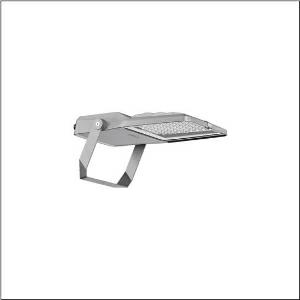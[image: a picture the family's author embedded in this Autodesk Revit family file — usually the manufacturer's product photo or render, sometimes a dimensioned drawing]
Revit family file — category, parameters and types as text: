
# Revit family: floodlight_fl_21_iq_mini___pl61_5xa7772b2c1a_d28a
name_source: partatom
category: Lighting Fixtures
units: mm (PartAtom-declared; Revit-internal decimal feet)

## family parameters
Cut with Voids When Loaded = No
Host = Face
Light Source = No
Part Type = Normal
Room Calculation Point = No
Round Connector Dimension = Use Diameter
Shared = No

## types (1)
- --- (1 x LED, 6120 lm, 45.5 W, 3000K)
    Apparent Load = 46 VA
    CIE Flux Codes = 33 65 98 100 100
    Color Rendering = 70
    Color Temperature = 3000K
    Default Elevation = 1800 mm
    Description = Floodlight FL 21 iQ mini, floodlight, primary light control with lens, of PMMA, primary optical cover: protective disc, of toughened safety glass, transparent, light distribution: PL61, light emission: direct distribution, installation type: surface-mounted, lamps: LED, High Power LED, rated values: 6.120lm | 45,5W | 134,5lm/W (begin service life); end service life: 6.120lm | 48W; at 50% lumin. flux: 3.060lm | 21,5W | 142,3lm/W, colour temperature: 3000K, colour rendering: CRI > 70, light colour: 730, light setting 1 begin service life: 100% | 6.120lm | 45,5W | 134,5lm/W | 3.000K, light setting 1 end service life: 48W, further light settings possible, control: Street-Remote, Auto-Match, Temp-Guard, Night-Set, Smart-Wire, Desk-Remote (wireless, voltage-free reading and setting of iQ features in the workshop via application-optimized NFC function/RFID function), optimised constant luminous flux control (CLO 2.0), pre-setting: linear dimming characteristic, with terminal, 6-pole, mains connection: 220..240V, AC, 50/60Hz, luminaire housing, of diecast aluminium, powder-coated, SITECO metallic grey (DB 702S), corrosivity category C5 mid according to DIN EN ISO 12944suitable for swimming poolschlorine-resistant, sealing non-destructively replaceable, mounting bracket, of steel, galvanised, powder-coated, SITECO metallic grey (DB 702S), protection rating (complete): IP66, insulation class (complete): insulation class II (safety insulation), certification: CE, ENEC, VDE, protection symbol: D, impact resistance: IK08, permissible operating ambient temperature: -40..+40°C, permissible operating ambient temperature for outdoor applications: -40..+50°C, standard: DIN EN 12944, LABS conformity tested according to VDMA 24364:2018-05, packaging unit: 1 piece

Light Distribution: PL61
    Height = 70 mm
    Lamp = 1 x LED
    Lamp Light Flux = 6120 lm
    Lamp Power = 45.5 W
    Lamp count = 1
    Length = 485 mm
    Luminous efficacy = 135 lm/W
    Manufacturer = Siteco
    ModVariant = No
    Model = 5XA7772B2C1A
    Number of Poles = 1
    OnlyDefault = Yes
    Power Factor = 1
    Product Name = Floodlight FL 21 iQ mini | PL61
    Product group = floodlight | pylon annexe
    ProductGroupID = 6201
    Protection Class = Protection class II
    Protection Degree = IP 66
    RLX_Detail_Level = 1
    RLX_Emergency_Light_Flux = 0 lm
    RLX_Emergency_Type = 0
    RLX_Emergency_Type_DB = No
    RlxData = <blob elided: 96737 chars, md5=e33921dc>
    Socket = socket
    Standby Power = 0 W
    System Light Flux = 6120 lm
    System Power = 46 W
    Type Comments = factory setting: luminous flux: 100 % | dim-lin: 254 | 463 mA
    Type Image = l_1006845.jpg
    URL = http://relux.com
    VarID = @adj_173141
    Voltage = 0 V
    Weight = 0.00 kg
    Width = 337 mm

## geometry (parser evidence)
native form markers: Blend x4, Sweep x11
no freeform markers — native parametric forms only
